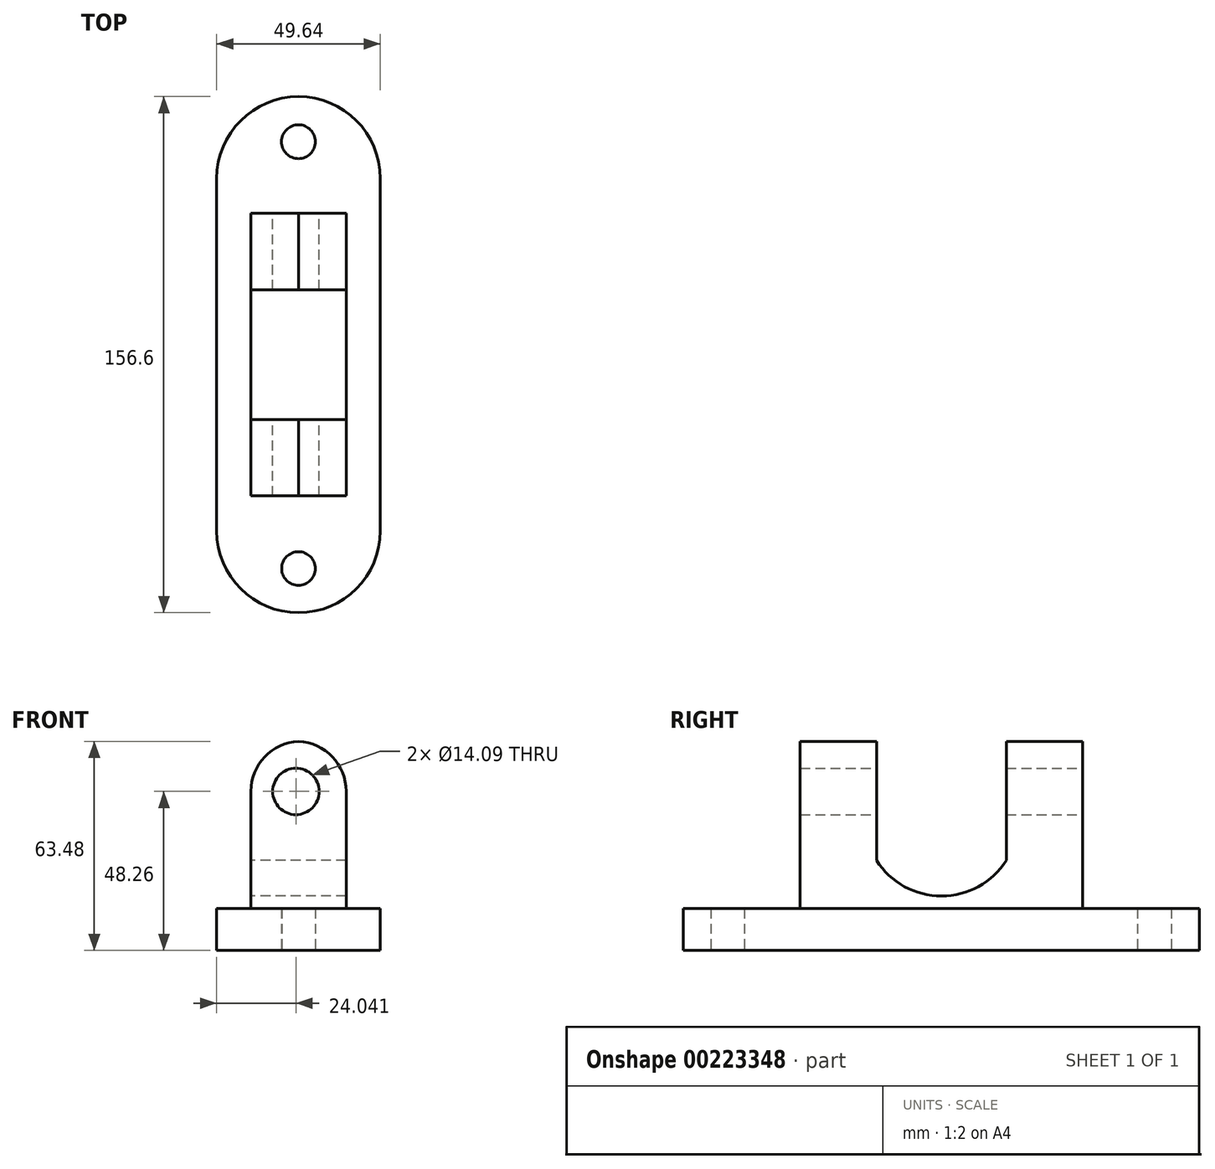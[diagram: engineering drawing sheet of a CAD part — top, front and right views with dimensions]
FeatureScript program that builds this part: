
annotation { "Feature Type Name" : "Feature", "Feature Type Description" : "" }
export const myFeature = defineFeature(function(context is Context, id is Id, definition is map)
    precondition{}
    {
        {
            var Q0;
            Q0=qCreatedBy(makeId("Top.planeOp"),FACE);
            var sketch = newSketch(context, id + "F0", { "sketchPlane" : qUnion([Q0])});
            skLineSegment(sketch, "E0.bottom", {"start": v(-24.82, 53.48) * mm, "end": v(24.82, 53.48) * mm});
            skLineSegment(sketch, "E0.top", {"start": v(-24.82, -53.48) * mm, "end": v(24.82, -53.48) * mm});
            skLineSegment(sketch, "E0.left", {"start": v(-24.82, 53.48) * mm, "end": v(-24.82, -53.48) * mm});
            skLineSegment(sketch, "E0.right", {"start": v(24.82, 53.48) * mm, "end": v(24.82, -53.48) * mm});
            skPoint(sketch, "E0.middle", {"position": v(0, 0) * mm});
            skArc(sketch, "E1", {"start": v(24.82, 53.48) * mm, "mid": v(0, 78.3) * mm, "end": v(-24.82, 53.48) * mm});
            skArc(sketch, "E2", {"start": v(-24.82, -53.48) * mm, "mid": v(0, -78.3) * mm, "end": v(24.82, -53.48) * mm});
            skCircle(sketch, "E3", {"center": v(0, 64.6) * mm, "radius": 5.14 * mm});
            skCircle(sketch, "E4", {"center": v(0, -64.9) * mm, "radius": 5.1 * mm});
            skSolve(sketch);
        }
        {
            var Q0;
            Q0 = qSketchRegion(id + "F0", true);
            extrude(context, id + "F1", {"entities" : qUnion([Q0]), "depth" : 12.7 * mm});
        }
        {
            var Q0;
            Q0=makeQuery(id+"F1.opExtrude","CAP_FACE",FACE,{"disambiguationData":[OSD([sQuery(id+"F0.wireOp",EDGE,"E0.left"),sQuery(id+"F0.wireOp",EDGE,"E0.right"),sQuery(id+"F0.wireOp",EDGE,"E1"),sQuery(id+"F0.wireOp",EDGE,"E2"),sQuery(id+"F0.wireOp",EDGE,"E3"),sQuery(id+"F0.wireOp",EDGE,"E4")])],"isStart":false});
            var sketch = newSketch(context, id + "F2", { "sketchPlane" : qUnion([Q0])});
            skLineSegment(sketch, "E5.bottom", {"start": v(-14.46, 42.86) * mm, "end": v(14.46, 42.86) * mm});
            skLineSegment(sketch, "E5.top", {"start": v(-14.46, -42.86) * mm, "end": v(14.46, -42.86) * mm});
            skLineSegment(sketch, "E5.left", {"start": v(-14.46, 42.86) * mm, "end": v(-14.46, -42.86) * mm});
            skLineSegment(sketch, "E5.right", {"start": v(14.46, 42.86) * mm, "end": v(14.46, -42.86) * mm});
            skPoint(sketch, "E5.middle", {"position": v(0, 0) * mm});
            skSolve(sketch);
        }
        {
            var Q0;
            Q0 = qSketchRegion(id + "F2", true);
            extrude(context, id + "F3", {"entities" : qUnion([Q0]), "operationType" : NewBodyOperationType.ADD, "depth" : 50.8 * mm});
        }
        {
            var Q0;
            Q0=makeQuery(id+"F3.opExtrude","CAP_EDGE",EDGE,{"disambiguationData":[OSD([sQuery(id+"F2.wireOp",EDGE,"E5.right")])],"isStart":false});
            var Q1;
            Q1=makeQuery(id+"F3.opExtrude","CAP_EDGE",EDGE,{"disambiguationData":[OSD([sQuery(id+"F2.wireOp",EDGE,"E5.left")])],"isStart":false});
            fillet(context, id + "F4", {"entities" : qUnion([Q0, Q1]), "radius" : 15.24 * mm, "allowEdgeOverflow" : false});
        }
        {
            var Q0;
            Q0=makeQuery(id+"F3.opExtrude","SWEPT_FACE",FACE,{"disambiguationData":[OSD([sQuery(id+"F2.wireOp",EDGE,"E5.bottom")])]});
            var sketch = newSketch(context, id + "F5", { "sketchPlane" : qUnion([Q0])});
            skCircle(sketch, "E6", {"center": v(0.78, 48.26) * mm, "radius": 7.05 * mm});
            skSolve(sketch);
        }
        {
            var Q0;
            Q0 = qSketchRegion(id + "F5", true);
            extrude(context, id + "F6", {"entities" : qUnion([Q0]), "operationType" : NewBodyOperationType.REMOVE, "oppositeDirection" : true, "depth" : 101.6 * mm});
        }
        {
            var Q0;
            Q0=makeQuery(id+"F3.opExtrude","SWEPT_FACE",FACE,{"disambiguationData":[OSD([sQuery(id+"F2.wireOp",EDGE,"E5.left")])]});
            var sketch = newSketch(context, id + "F7", { "sketchPlane" : qUnion([Q0])});
            skLineSegment(sketch, "E7.bottom", {"start": v(-19.68, 69.17) * mm, "end": v(19.68, 69.17) * mm});
            skLineSegment(sketch, "E7.top", {"start": v(-19.68, 27.35) * mm, "end": v(19.68, 27.35) * mm});
            skLineSegment(sketch, "E7.left", {"start": v(-19.68, 69.17) * mm, "end": v(-19.68, 27.35) * mm});
            skLineSegment(sketch, "E7.right", {"start": v(19.68, 69.17) * mm, "end": v(19.68, 27.35) * mm});
            skPoint(sketch, "E7.middle", {"position": v(0, 48.26) * mm});
            skArc(sketch, "E8", {"start": v(-19.68, 27.35) * mm, "mid": v(0, 16.52) * mm, "end": v(19.68, 27.35) * mm});
            skSolve(sketch);
        }
        {
            var Q0;
            Q0 = qSketchRegion(id + "F7", true);
            extrude(context, id + "F8", {"entities" : qUnion([Q0]), "operationType" : NewBodyOperationType.REMOVE, "oppositeDirection" : true, "depth" : 50.8 * mm, "hasSecondDirection" : true, "secondDirectionOppositeDirection" : false, "secondDirectionDepth" : 25.4 * mm});
        }
    });
